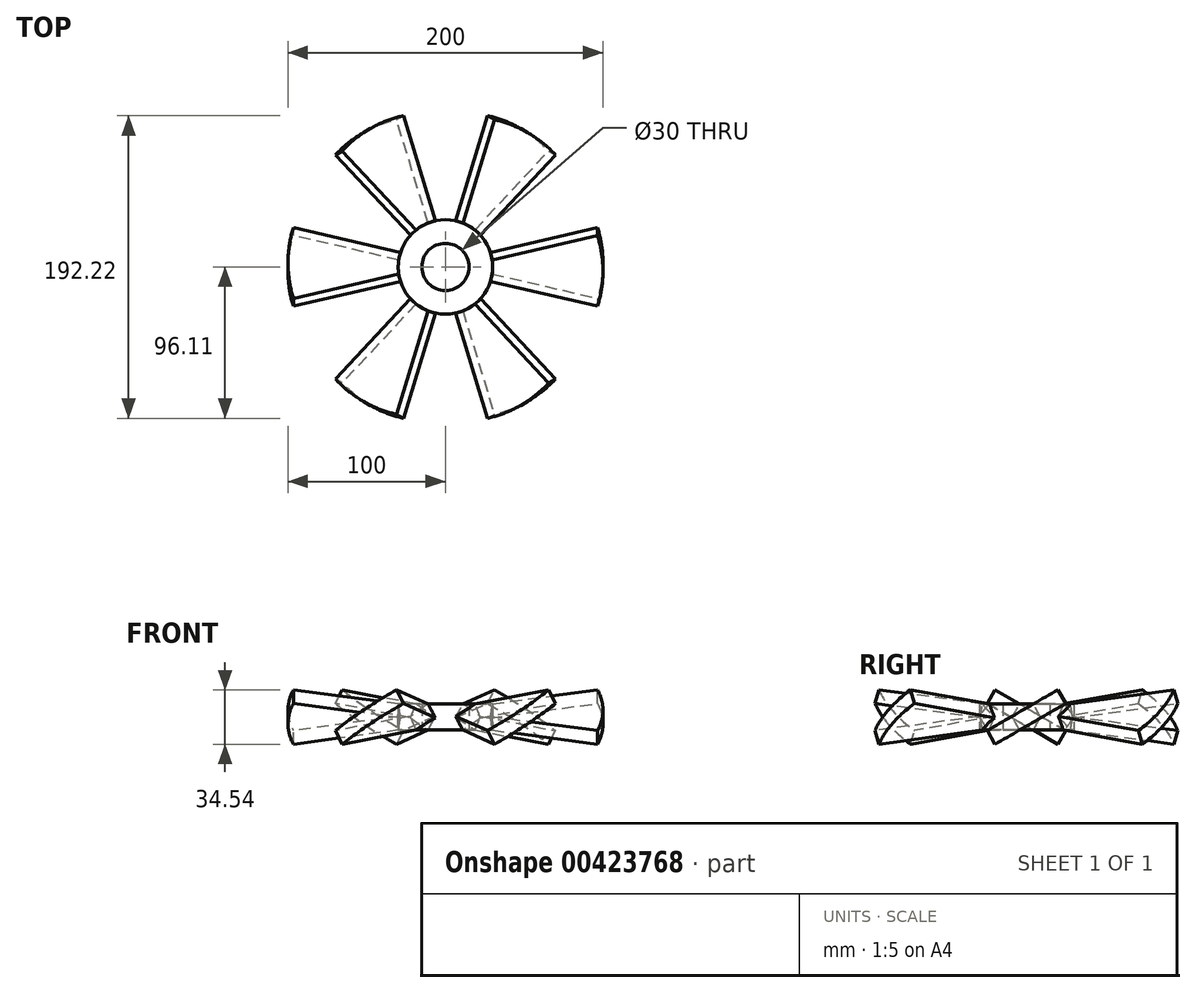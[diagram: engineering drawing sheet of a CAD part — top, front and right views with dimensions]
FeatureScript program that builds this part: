
annotation { "Feature Type Name" : "Feature", "Feature Type Description" : "" }
export const myFeature = defineFeature(function(context is Context, id is Id, definition is map)
    precondition{}
    {
        {
            var Q0;
            Q0=qCreatedBy(makeId("Top.planeOp"),FACE);
            var sketch = newSketch(context, id + "F0", { "sketchPlane" : qUnion([Q0])});
            skLineSegment(sketch, "E0", {"start": v(0, 0) * mm, "end": v(83.36, 0) * mm, "construction": true});
            skSolve(sketch);
        }
        {
            var Q0;
            Q0=sQuery(id+"F0.wireOp",EDGE,"E0");
            cPlane(context, id + "F1", {"entities" : qUnion([Q0]), "cplaneType" : CPlaneType.LINE_ANGLE, "offset" : 25 * mm, "angle" : 60 * degree, "oppositeDirection" : true, "width" : 150 * mm, "height" : 150 * mm});
        }
        {
            var Q0;
            Q0=qCreatedBy(id+"F1.planeOp",FACE);
            var sketch = newSketch(context, id + "F2", { "sketchPlane" : qUnion([Q0])});
            skArc(sketch, "E1", {"start": v(96.6, -25.88) * mm, "mid": v(100, 0) * mm, "end": v(96.6, 25.88) * mm});
            skLineSegment(sketch, "E2", {"start": v(28.98, -7.76) * mm, "end": v(96.6, -25.88) * mm});
            skLineSegment(sketch, "E3.MirrorCS", {"start": v(28.98, 7.76) * mm, "end": v(96.6, 25.88) * mm});
            skLineSegment(sketch, "E4", {"start": v(28.98, -7.76) * mm, "end": v(0, 0) * mm});
            skLineSegment(sketch, "E5", {"start": v(28.98, 7.76) * mm, "end": v(0, 0) * mm});
            skSolve(sketch);
        }
        {
            var Q0;
            Q0=qCreatedBy(makeId("Top.planeOp"),FACE);
            var sketch = newSketch(context, id + "F3", { "sketchPlane" : qUnion([Q0])});
            skCircle(sketch, "E6", {"center": v(0, 0) * mm, "radius": 30 * mm});
            skSolve(sketch);
        }
        {
            var Q0;
            Q0=qCreatedBy(makeId("Front.planeOp"),FACE);
            var sketch = newSketch(context, id + "F4", { "sketchPlane" : qUnion([Q0])});
            skLineSegment(sketch, "E7", {"start": v(0, -81.33) * mm, "end": v(0, 84.03) * mm});
            skSolve(sketch);
        }
        {
            var Q0;
            Q0=makeQuery(id+"F2.imprint","IMPRINT",FACE,{"disambiguationData":[TD([[makeQuery(id+"F2.imprint","IMPRINT",EDGE,{"derivedFrom":sQuery(id+"F2.wireOp",EDGE,"E1")}),1.0]])]});
            extrude(context, id + "F5", {"entities" : qUnion([Q0]), "endBound" : BoundingType.SYMMETRIC, "depth" : 10 * mm});
        }
        {
            var Q0;
            Q0=makeQuery(id+"F3.imprint","IMPRINT",FACE,{"disambiguationData":[TD([[makeQuery(id+"F3.imprint","IMPRINT",EDGE,{"derivedFrom":sQuery(id+"F3.wireOp",EDGE,"E6")}),1.0]])]});
            extrude(context, id + "F6", {"entities" : qUnion([Q0]), "operationType" : NewBodyOperationType.REMOVE, "endBound" : BoundingType.SYMMETRIC, "oppositeDirection" : true, "depth" : 25 * mm});
        }
        {
            var Q0;
            Q0=makeQuery(id+"F5.opExtrude","SWEPT_BODY",BODY,{"disambiguationData":[OSD([sQuery(id+"F2.wireOp",EDGE,"E1"),sQuery(id+"F2.wireOp",EDGE,"E2"),sQuery(id+"F2.wireOp",EDGE,"E3.MirrorCS"),sQuery(id+"F2.wireOp",EDGE,"E4"),sQuery(id+"F2.wireOp",EDGE,"E5")])]});
            var Q1;
            Q1=sQuery(id+"F4.wireOp",EDGE,"E7");
            circularPattern(context, id + "F7", {"entities" : qUnion([Q0]), "axis" : qUnion([Q1]), "angle" : 360 * degree, "instanceCount" : 6, "equalSpace" : true});
        }
        {
            var Q0;
            Q0=qCreatedBy(makeId("Top.planeOp"),FACE);
            var sketch = newSketch(context, id + "F8", { "sketchPlane" : qUnion([Q0])});
            skCircle(sketch, "E8", {"center": v(0, 0) * mm, "radius": 15 * mm});
            skCircle(sketch, "E9", {"center": v(0, 0) * mm, "radius": 30 * mm});
            skSolve(sketch);
        }
        {
            var Q0;
            Q0=makeQuery(id+"F8.imprint","IMPRINT",FACE,{"disambiguationData":[TD([[makeQuery(id+"F8.imprint","IMPRINT",EDGE,{"derivedFrom":sQuery(id+"F8.wireOp",EDGE,"E8")}),-1.0]])]});
            extrude(context, id + "F9", {"entities" : qUnion([Q0]), "depth" : 8.3 * mm, "hasSecondDirection" : true, "secondDirectionOppositeDirection" : true, "secondDirectionDepth" : 8.3 * mm});
        }
    });
